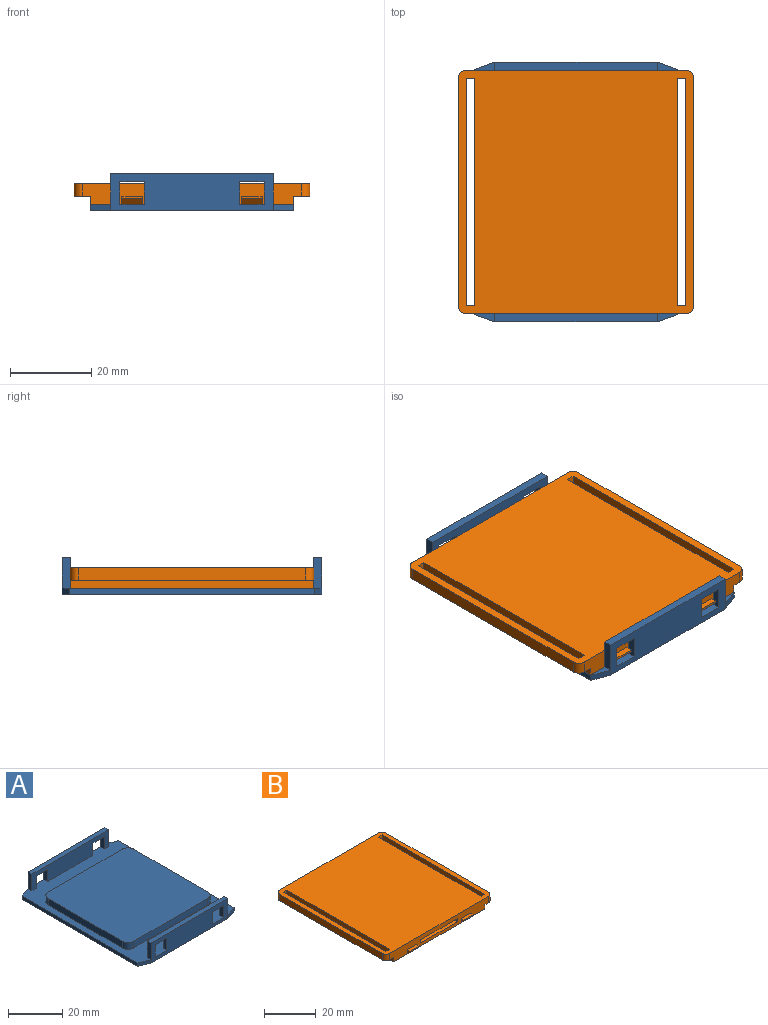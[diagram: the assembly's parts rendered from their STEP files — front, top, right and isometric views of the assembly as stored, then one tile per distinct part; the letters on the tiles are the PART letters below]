
ASSEMBLY  parts=2 mates=1
PART A: 39 faces, bbox 50x64x9 mm
  f0: plane 64x50mm, normal (0,0,1), area 1097.3mm2, adj f1,f2,f4,f5,f6,f7,f9,f10
  f1: plane 60.36x1.5mm, normal (1,0,0), area 90.5mm2, adj f0,f3,f36,f37
  f2: plane 60.36x1.5mm, normal (-1,0,0), area 90.5mm2, adj f0,f3,f35,f38
  f3: plane 64x50mm, normal (0,0,-1), area 3181.8mm2, adj f1,f2,f4,f10,f35,f36,f37,f38
  f4: plane 40x9mm, normal (0,1,0), area 294mm2, adj f0,f3,f5,f7,f8,f20,f21,f22
  f5: plane 7.5x2mm, normal (-1,0,0), area 15mm2, adj f0,f4,f6,f8
  f6: plane 40x7.5mm, normal (0,-1,0), area 234mm2, adj f0,f5,f7,f8,f20,f21,f22,f23
  f7: plane 7.5x2mm, normal (1,0,0), area 15mm2, adj f0,f4,f6,f8
  f8: plane 40x2mm, normal (0,0,1), area 80mm2, adj f4,f5,f6,f7
  f9: plane 40x7.5mm, normal (0,1,0), area 234mm2, adj f0,f11,f12,f13,f14,f15,f16,f17
  f10: plane 40x9mm, normal (0,-1,0), area 294mm2, adj f0,f3,f11,f12,f13,f14,f15,f16
  f11: plane 7.5x2mm, normal (1,0,0), area 15mm2, adj f0,f9,f10,f13
  f12: plane 7.5x2mm, normal (-1,0,0), area 15mm2, adj f0,f9,f10,f13
  f13: plane 40x2mm, normal (0,0,1), area 80mm2, adj f9,f10,f11,f12
  f14: plane 5.5x2mm, normal (-1,0,0), area 11mm2, adj f0,f9,f10,f16
  f15: plane 5.5x2mm, normal (1,0,0), area 11mm2, adj f0,f9,f10,f16
  f16: plane 6x2mm, normal (0,0,-1), area 12mm2, adj f9,f10,f14,f15
  f17: plane 6x2mm, normal (0,0,-1), area 12mm2, adj f9,f10,f18,f19
  f18: plane 5.5x2mm, normal (-1,0,0), area 11mm2, adj f0,f9,f10,f17
  f19: plane 5.5x2mm, normal (1,0,0), area 11mm2, adj f0,f9,f10,f17
  f20: plane 6x2mm, normal (0,0,-1), area 12mm2, adj f4,f6,f21,f22
  f21: plane 5.5x2mm, normal (1,0,0), area 11mm2, adj f0,f4,f6,f20
  f22: plane 5.5x2mm, normal (-1,0,0), area 11mm2, adj f0,f4,f6,f20
  f23: plane 5.5x2mm, normal (1,0,0), area 11mm2, adj f0,f4,f6,f25
  f24: plane 5.5x2mm, normal (-1,0,0), area 11mm2, adj f0,f4,f6,f25
  f25: plane 6x2mm, normal (0,0,-1), area 12mm2, adj f4,f6,f23,f24
  f26: plane 38.5x3mm, normal (1,0,0), area 115.5mm2, adj f0,f30,f31,f34
  f27: plane 38.5x3mm, normal (0,1,0), area 115.5mm2, adj f0,f30,f31,f32
  f28: plane 38.5x3mm, normal (-1,0,0), area 115.5mm2, adj f0,f30,f32,f33
  f29: plane 38.5x3mm, normal (0,-1,0), area 115.5mm2, adj f0,f30,f33,f34
  f30: plane 44.5x44.5mm, normal (0,0,1), area 1972.5mm2, adj f26,f27,f28,f29,f31,f32,f33,f34
  f31: cylinder r=3mm len=3mm, axis (0,0,-1), area 14.1mm2, adj f0,f26,f27,f30
  f32: cylinder r=3mm len=3mm, axis (0,0,1), area 14.1mm2, adj f0,f27,f28,f30
  f33: cylinder r=3mm len=3mm, axis (0,0,-1), area 14.1mm2, adj f0,f28,f29,f30
  f34: cylinder r=3mm len=3mm, axis (0,0,1), area 14.1mm2, adj f0,f26,f29,f30
  f35: plane 5x1.82mm, normal (-0.34,-0.94,0), area 8mm2, adj f0,f2,f3,f10
  f36: plane 5x1.82mm, normal (0.34,0.94,0), area 8mm2, adj f0,f1,f3,f4
  f37: plane 5x1.82mm, normal (0.34,-0.94,0), area 8mm2, adj f0,f1,f3,f10
  f38: plane 5x1.82mm, normal (-0.34,0.94,0), area 8mm2, adj f0,f2,f3,f4
PART B: 48 faces, bbox 58x63x5 mm
  f0: plane 54x5mm, normal (0,1,0), area 242mm2, adj f2,f3,f5,f6,f7,f9,f25,f26
  f1: plane 54x5mm, normal (0,-1,0), area 212mm2, adj f2,f3,f5,f6,f7,f9,f14,f15
  f2: plane 60x58mm, normal (0,0,1), area 3252.6mm2, adj f0,f1,f5,f6,f8,f10,f18,f19
  f3: plane 60x4mm, normal (0,0,-1), area 126.3mm2, adj f0,f1,f5,f10,f18,f19,f20,f24
  f4: plane 45.5x3mm, normal (0,1,0), area 106.5mm2, adj f7,f11,f13,f14,f15,f16,f17
  f5: plane 60x5mm, normal (1,0,0), area 288mm2, adj f0,f1,f2,f3,f7,f18,f20
  f6: plane 60x5mm, normal (-1,0,0), area 288mm2, adj f0,f1,f2,f7,f9,f21,f22
  f7: plane 60x50mm, normal (0,0,-1), area 929.8mm2, adj f0,f1,f4,f5,f6,f11,f12,f13
  f8: plane 56x3mm, normal (-1,0,0), area 168mm2, adj f2,f9,f26,f27
  f9: plane 60x4mm, normal (0,0,-1), area 126.3mm2, adj f0,f1,f6,f8,f21,f22,f23,f26
  f10: plane 56x3mm, normal (1,0,0), area 168mm2, adj f2,f3,f24,f25
  f11: plane 45.5x3mm, normal (-1,0,0), area 136.5mm2, adj f4,f7,f12,f14
  f12: plane 45.5x3mm, normal (0,-1,0), area 136.5mm2, adj f7,f11,f13,f14
  f13: plane 45.5x3mm, normal (1,0,0), area 136.5mm2, adj f4,f7,f12,f14
  f14: plane 52.75x45.5mm, normal (0,0,-1), area 2215.2mm2, adj f1,f4,f11,f12,f13,f15,f16
  f15: plane 7.25x1.5mm, normal (-1,0,0), area 10.9mm2, adj f1,f4,f14,f17
  f16: plane 7.25x1.5mm, normal (1,0,0), area 10.9mm2, adj f1,f4,f14,f17
  f17: plane 20x7.25mm, normal (0,0,1), area 145mm2, adj f1,f4,f15,f16
  f18: plane 3x2mm, normal (0,1,0), area 6mm2, adj f2,f3,f5,f19
  f19: plane 56x3mm, normal (-1,0,0), area 168mm2, adj f2,f3,f18,f20
  f20: plane 3x2mm, normal (0,-1,0), area 6mm2, adj f2,f3,f5,f19
  f21: plane 3x2mm, normal (0,1,0), area 6mm2, adj f2,f6,f9,f23
  f22: plane 3x2mm, normal (0,-1,0), area 6mm2, adj f2,f6,f9,f23
  f23: plane 56x3mm, normal (1,0,0), area 168mm2, adj f2,f9,f21,f22
  f24: cylinder r=2mm len=3mm, axis (0,0,-1), area 9.4mm2, adj f1,f2,f3,f10
  f25: cylinder r=2mm len=3mm, axis (0,0,1), area 9.4mm2, adj f0,f2,f3,f10
  f26: cylinder r=2mm len=3mm, axis (0,0,-1), area 9.4mm2, adj f0,f2,f8,f9
  f27: cylinder r=2mm len=3mm, axis (0,0,1), area 9.4mm2, adj f1,f2,f8,f9
  f28: plane 2x1.5mm, normal (-1,0,0), area 1.9mm2, adj f1,f29,f31,f47
  f29: plane 5x0.5mm, normal (0,-1,0), area 2.5mm2, adj f28,f30,f31,f47
  f30: plane 2x1.5mm, normal (1,0,0), area 1.9mm2, adj f1,f29,f31,f47
  f31: plane 5x1.5mm, normal (0,0,1), area 7.5mm2, adj f1,f28,f29,f30
  f32: plane 5x0.5mm, normal (0,-1,0), area 2.5mm2, adj f33,f34,f35,f46
  f33: plane 2x1.5mm, normal (1,0,0), area 1.9mm2, adj f1,f32,f35,f46
  f34: plane 2x1.5mm, normal (-1,0,0), area 1.9mm2, adj f1,f32,f35,f46
  f35: plane 5x1.5mm, normal (0,0,1), area 7.5mm2, adj f1,f32,f33,f34
  f36: plane 2x1.5mm, normal (1,0,0), area 1.9mm2, adj f0,f37,f39,f45
  f37: plane 5x0.5mm, normal (0,1,0), area 2.5mm2, adj f36,f38,f39,f45
  f38: plane 2x1.5mm, normal (-1,0,0), area 1.9mm2, adj f0,f37,f39,f45
  f39: plane 5x1.5mm, normal (0,0,1), area 7.5mm2, adj f0,f36,f37,f38
  f40: plane 2x1.5mm, normal (-1,0,0), area 1.9mm2, adj f0,f42,f43,f44
  f41: plane 2x1.5mm, normal (1,0,0), area 1.9mm2, adj f0,f42,f43,f44
  f42: plane 5x0.5mm, normal (0,1,0), area 2.5mm2, adj f40,f41,f43,f44
  f43: plane 5x1.5mm, normal (0,0,1), area 7.5mm2, adj f0,f40,f41,f42
  f44: plane 5x1.5mm, normal (0,0.71,-0.71), area 10.6mm2, adj f7,f40,f41,f42
  f45: plane 5x1.5mm, normal (0,0.71,-0.71), area 10.6mm2, adj f7,f36,f37,f38
  f46: plane 5x1.5mm, normal (0,-0.71,-0.71), area 10.6mm2, adj f7,f32,f33,f34
  f47: plane 5x1.5mm, normal (0,-0.71,-0.71), area 10.6mm2, adj f7,f28,f29,f30
PLACE A rot(axis=(0,0,1),0deg) t=(4.26,-14.8,-8.77)mm
PLACE B rot(axis=(0,0,1),0deg) t=(4.26,-14.8,-7.27)mm
MATE slider A.f30 <-> B.f7  axis (0,0,1) through (4.26,-14.8,-4.27)mm
